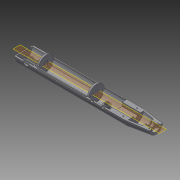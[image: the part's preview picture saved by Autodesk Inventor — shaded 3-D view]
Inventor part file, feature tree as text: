
AUTODESK INVENTOR PART (.ipt)
format: ipt  version: 2014 (Build 180170000, 170)  size: 548,864 bytes
history: native  units: mm
features: sketch x31, extrude x30, other x9, projected_geometry x3, fillet x2, loft x1
ambient origin geometry x8: Origin, YZ Plane, XZ Plane, XY Plane, X Axis, Y Axis, Z Axis, Center Point
bodies: Body1 (feature_tree)
feature tree (76):
  other  "Твердое тело1"
  extrude  "Выдавливание1"  Depth=11.0mm
  other  "РабПлоскость1"
  sketch  "Эскиз3"
  extrude  "Выдавливание2"  Depth=13.0mm
  loft  "Лофт2"
  extrude  "Выдавливание3"  Depth=180.0mm
  extrude  "Выдавливание4"  Depth=9.0mm
  extrude  "Выдавливание_Стойки"  Depth=6.0mm
  other  "РабПлоскость2"
  extrude  "Выдавливание Кнопки"  Depth=1.2mm TaperAngle=0.0deg
  fillet  "Сопряжение Торец копуса"  [1 undecoded]
  other  "РабПлоскость3"
  extrude  "Выдавливание7"  TaperAngle=0.0deg  [1 undecoded]
  extrude  "Выдавливание8"  Depth=1.5mm
  extrude  "Выдавливание9"  Depth=0.8mm
  other  "РабПлоскость4"
  extrude  "Выдавливание10"  Depth=1.0mm
  extrude  "Выдавливание11"  Depth=28.0mm TaperAngle=0.0deg
  other  "РабПлоскость5 Середина корпуса"
  extrude  "Выдавливание12"  Depth=4.0mm
  extrude  "Выдавливание13"  Depth=3.0mm
  extrude  "Выдавливание14"  Depth=2.0mm TaperAngle=0.0deg
  extrude  "Выдавливание15"  Depth=1.5mm
  extrude  "Выдавливание16"  Depth=4.0mm
  extrude  "Выдавливание17"  Depth=4.0mm
  extrude  "Выдавливание18"  Depth=25.0mm
  extrude  "Выдавливание19"  Depth=120.0mm
  extrude  "Выдавливание20"  Depth=1.5mm
  extrude  "Выдавливание21"  Depth=1.5mm
  other  "Выступ1"
  other  "Выступ2"
  extrude  "Выдавливание22"  Depth=11.0mm
  fillet  "Сопряжение4"  Radius=11.0mm
  extrude  "Выдавливание23"  Depth=4.0mm
  extrude  "Выдавливание24"  Depth=4.0mm
  extrude  "Выдавливание25"  Depth=15.0mm
  extrude  "Выдавливание26"  Depth=10.0mm TaperAngle=0.0deg
  extrude  "Выдавливание27"  Depth=2.0mm
  extrude  "Выдавливание28"  Depth=15.0mm
  extrude  "Выдавливание29"  Depth=2.0mm
  extrude  "Выдавливание30"  Depth=3.0mm
  sketch  "Эскиз1"
  sketch  "Эскиз4"
  other  "Ребра2"
  sketch  "Эскиз5"
  sketch  "Эскиз6"
  sketch  "Эскиз7"
  sketch  "Эскиз8"
  sketch  "Эскиз9"
  sketch  "Эскиз10"
  sketch  "Эскиз11"
  sketch  "Эскиз13"
  sketch  "Эскиз14"
  sketch  "Эскиз18"
  sketch  "Эскиз19"
  sketch  "Эскиз20"
  projected_geometry  "Спроецированная петля1"
  sketch  "Эскиз21"
  sketch  "Эскиз22"
  projected_geometry  "Спроецированная петля2"
  sketch  "Эскиз23"
  sketch  "Эскиз24"
  projected_geometry  "Спроецированная петля3"
  sketch  "Эскиз25"
  sketch  "Эскиз26"
  sketch  "Эскиз27"
  sketch  "Эскиз28"
  sketch  "Эскиз29"
  sketch  "Эскиз30"
  sketch  "Эскиз31"
  sketch  "Эскиз32"
  sketch  "Эскиз33"
  sketch  "Эскиз34"
  sketch  "Эскиз35"
  sketch  "Эскиз36"
note: 2 required parameter values undecoded (feature->parameter linkage not recoverable at this tier; creation-order binding heuristic only, values carry confidence <= 0.55)
